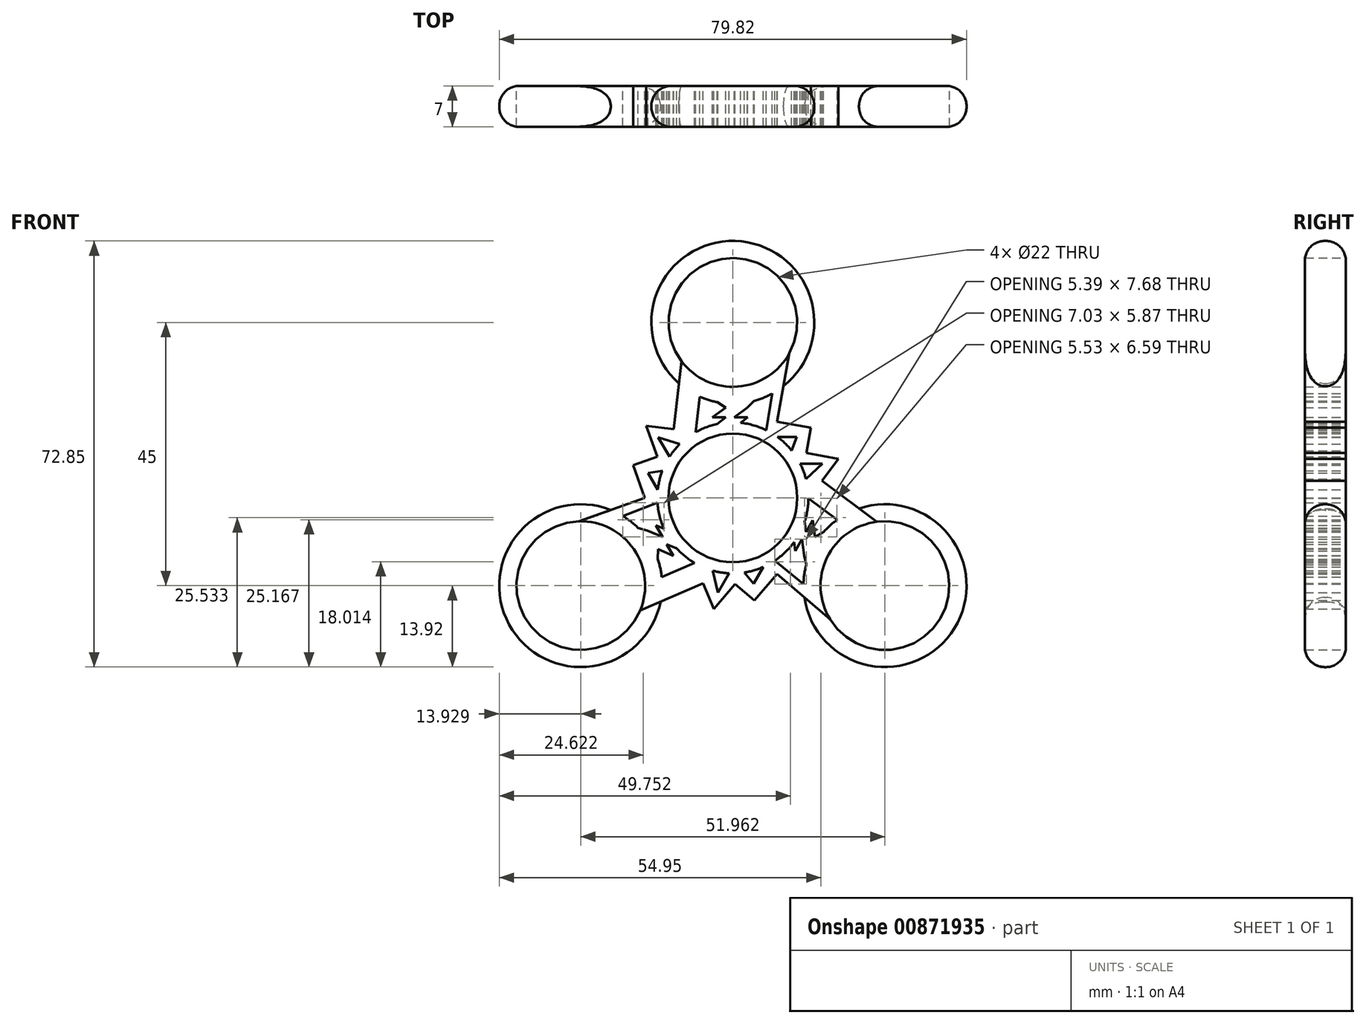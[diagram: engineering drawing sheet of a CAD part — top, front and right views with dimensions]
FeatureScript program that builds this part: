
annotation { "Feature Type Name" : "Feature", "Feature Type Description" : "" }
export const myFeature = defineFeature(function(context is Context, id is Id, definition is map)
    precondition{}
    {
        {
            var Q0;
            Q0=qCreatedBy(makeId("Front.planeOp"),FACE);
            var sketch = newSketch(context, id + "F0", { "sketchPlane" : qUnion([Q0])});
            skCircle(sketch, "E0", {"center": v(0, 0) * mm, "radius": 11 * mm});
            skSolve(sketch);
        }
        {
            var Q0;
            Q0=qCreatedBy(makeId("Front.planeOp"),FACE);
            var sketch = newSketch(context, id + "F1", { "sketchPlane" : qUnion([Q0])});
            skCircle(sketch, "E1", {"center": v(0, 30) * mm, "radius": 11 * mm});
            skCircle(sketch, "E2.1.0", {"center": v(-25.98, -15) * mm, "radius": 11 * mm});
            skCircle(sketch, "E2.2.0", {"center": v(25.98, -15) * mm, "radius": 11 * mm});
            skPoint(sketch, "E2.center", {"position": v(0, 0) * mm});
            skSolve(sketch);
        }
        {
            var Q0;
            Q0=qCreatedBy(makeId("Front.planeOp"),FACE);
            var sketch = newSketch(context, id + "F2", { "sketchPlane" : qUnion([Q0])});
            skArc(sketch, "E3", {"start": v(-2.7, 16.35) * mm, "mid": v(-0.48, 43.92) * mm, "end": v(3.63, 16.57) * mm});
            skLineSegment(sketch, "E4", {"start": v(3.63, 16.57) * mm, "end": v(2.45, 15.46) * mm});
            skLineSegment(sketch, "E5", {"start": v(-2.7, 16.35) * mm, "end": v(-1.21, 15.46) * mm});
            skLineSegment(sketch, "E6", {"start": v(-1.21, 15.46) * mm, "end": v(-2.7, 14.36) * mm});
            skLineSegment(sketch, "E7", {"start": v(2.45, 15.46) * mm, "end": v(0.22, 13.75) * mm});
            skLineSegment(sketch, "E8", {"start": v(0.22, 13.75) * mm, "end": v(2.54, 13.75) * mm});
            skLineSegment(sketch, "E9", {"start": v(-2.7, 14.36) * mm, "end": v(-3.51, 13.75) * mm});
            skLineSegment(sketch, "E10", {"start": v(-3.51, 13.75) * mm, "end": v(-1.21, 13.75) * mm});
            skLineSegment(sketch, "E11", {"start": v(-1.21, 13.75) * mm, "end": v(-2.7, 12.62) * mm});
            skArc(sketch, "E12", {"start": v(-2.7, 12.62) * mm, "mid": v(0.7, -12.88) * mm, "end": v(1.3, 12.84) * mm});
            skLineSegment(sketch, "E13", {"start": v(2.54, 13.75) * mm, "end": v(1.3, 12.84) * mm});
            skArc(sketch, "E14.1.0", {"start": v(-12.82, -10.5) * mm, "mid": v(-37.8, -22.38) * mm, "end": v(-16.17, -5.14) * mm});
            skLineSegment(sketch, "E14.1.1", {"start": v(-12.02, -6.69) * mm, "end": v(-13.18, -4.68) * mm});
            skLineSegment(sketch, "E14.1.2", {"start": v(-14.61, -5.61) * mm, "end": v(-12.02, -6.69) * mm});
            skLineSegment(sketch, "E14.1.3", {"start": v(-16.17, -5.14) * mm, "end": v(-14.61, -5.61) * mm});
            skLineSegment(sketch, "E14.1.4", {"start": v(-11.3, -7.93) * mm, "end": v(-9.58, -8.64) * mm});
            skLineSegment(sketch, "E14.1.5", {"start": v(-13.18, -4.68) * mm, "end": v(-11.77, -5.29) * mm});
            skLineSegment(sketch, "E14.1.6", {"start": v(-12.82, -10.5) * mm, "end": v(-12.78, -8.78) * mm});
            skLineSegment(sketch, "E14.1.7", {"start": v(-10.15, -9.92) * mm, "end": v(-11.3, -7.93) * mm});
            skLineSegment(sketch, "E14.1.8", {"start": v(-12.78, -8.78) * mm, "end": v(-11.1, -9.51) * mm});
            skLineSegment(sketch, "E14.1.9", {"start": v(-11.1, -9.51) * mm, "end": v(-10.15, -9.92) * mm});
            skArc(sketch, "E14.2.0", {"start": v(15.5, -5.85) * mm, "mid": v(38.28, -21.54) * mm, "end": v(12.54, -11.43) * mm});
            skLineSegment(sketch, "E14.2.1", {"start": v(11.8, -7.07) * mm, "end": v(10.64, -9.08) * mm});
            skLineSegment(sketch, "E14.2.2", {"start": v(12.17, -9.85) * mm, "end": v(11.8, -7.07) * mm});
            skLineSegment(sketch, "E14.2.3", {"start": v(12.54, -11.43) * mm, "end": v(12.17, -9.85) * mm});
            skLineSegment(sketch, "E14.2.4", {"start": v(12.52, -5.83) * mm, "end": v(12.27, -3.98) * mm});
            skLineSegment(sketch, "E14.2.5", {"start": v(10.64, -9.08) * mm, "end": v(10.46, -7.55) * mm});
            skLineSegment(sketch, "E14.2.6", {"start": v(15.5, -5.85) * mm, "end": v(14, -6.68) * mm});
            skLineSegment(sketch, "E14.2.7", {"start": v(13.67, -3.83) * mm, "end": v(12.52, -5.83) * mm});
            skLineSegment(sketch, "E14.2.8", {"start": v(14, -6.68) * mm, "end": v(13.79, -4.85) * mm});
            skLineSegment(sketch, "E14.2.9", {"start": v(13.79, -4.85) * mm, "end": v(13.67, -3.83) * mm});
            skSolve(sketch);
        }
        {
            var Q0;
            Q0=qCreatedBy(makeId("Front.planeOp"),FACE);
            var sketch = newSketch(context, id + "F3", { "sketchPlane" : qUnion([Q0])});
            skLineSegment(sketch, "E15", {"start": v(6.74, 17.86) * mm, "end": v(5.69, 11.3) * mm});
            skLineSegment(sketch, "E16", {"start": v(8.66, 19.26) * mm, "end": v(7.53, 13.05) * mm});
            skLineSegment(sketch, "E17", {"start": v(7.53, 13.05) * mm, "end": v(13.35, 11.98) * mm});
            skLineSegment(sketch, "E18", {"start": v(13.35, 11.98) * mm, "end": v(12.56, 7.67) * mm});
            skLineSegment(sketch, "E19", {"start": v(12.56, 7.67) * mm, "end": v(18.04, 6.66) * mm});
            skLineSegment(sketch, "E20", {"start": v(18.04, 6.66) * mm, "end": v(15.23, 2.9) * mm});
            skLineSegment(sketch, "E21", {"start": v(15.23, 2.9) * mm, "end": v(21.78, -2) * mm});
            skLineSegment(sketch, "E22", {"start": v(7.35, 10.42) * mm, "end": v(10.94, 10.42) * mm});
            skLineSegment(sketch, "E23", {"start": v(10.94, 10.42) * mm, "end": v(9.98, 7.88) * mm});
            skLineSegment(sketch, "E24", {"start": v(11.46, 5.87) * mm, "end": v(15.32, 5.87) * mm});
            skLineSegment(sketch, "E25", {"start": v(15.32, 5.87) * mm, "end": v(12.08, 2.9) * mm});
            skLineSegment(sketch, "E26", {"start": v(12.78, 0) * mm, "end": v(18.27, -4.1) * mm});
            skLineSegment(sketch, "E27", {"start": v(6.74, 17.86) * mm, "end": v(8.66, 19.26) * mm});
            skLineSegment(sketch, "E28", {"start": v(5.69, 11.3) * mm, "end": v(7.35, 10.42) * mm});
            skLineSegment(sketch, "E29", {"start": v(9.98, 7.88) * mm, "end": v(11.46, 5.87) * mm});
            skLineSegment(sketch, "E30", {"start": v(12.08, 2.9) * mm, "end": v(12.78, 0) * mm});
            skLineSegment(sketch, "E31", {"start": v(18.27, -4.1) * mm, "end": v(21.78, -2) * mm});
            skLineSegment(sketch, "E32.1.0", {"start": v(-17.05, 5.57) * mm, "end": v(-12.92, 7.04) * mm});
            skLineSegment(sketch, "E32.1.1", {"start": v(-15.06, 0) * mm, "end": v(-17.05, 5.57) * mm});
            skLineSegment(sketch, "E32.1.2", {"start": v(-18.84, -3.1) * mm, "end": v(-12.63, -0.72) * mm});
            skLineSegment(sketch, "E32.1.3", {"start": v(-12.92, 7.04) * mm, "end": v(-14.8, 12.3) * mm});
            skLineSegment(sketch, "E32.1.4", {"start": v(-12.74, 10.33) * mm, "end": v(-8.54, 9.01) * mm});
            skLineSegment(sketch, "E32.1.5", {"start": v(-6.39, 11.07) * mm, "end": v(-5.59, 17.86) * mm});
            skLineSegment(sketch, "E32.1.6", {"start": v(-10.12, 11.74) * mm, "end": v(-9.16, 19.86) * mm});
            skLineSegment(sketch, "E32.1.7", {"start": v(-14.8, 12.3) * mm, "end": v(-10.12, 11.74) * mm});
            skLineSegment(sketch, "E32.1.8", {"start": v(-8.54, 9.01) * mm, "end": v(-6.39, 11.07) * mm});
            skLineSegment(sketch, "E32.1.9", {"start": v(-21.01, -2.13) * mm, "end": v(-15.06, 0) * mm});
            skLineSegment(sketch, "E32.1.10", {"start": v(-12.7, 1.16) * mm, "end": v(-14.5, 4.26) * mm});
            skLineSegment(sketch, "E32.1.11", {"start": v(-5.59, 17.86) * mm, "end": v(-9.16, 19.86) * mm});
            skLineSegment(sketch, "E32.1.12", {"start": v(-10.81, 7) * mm, "end": v(-12.74, 10.33) * mm});
            skLineSegment(sketch, "E32.1.13", {"start": v(-14.5, 4.26) * mm, "end": v(-11.81, 4.7) * mm});
            skLineSegment(sketch, "E32.1.14", {"start": v(-18.84, -3.1) * mm, "end": v(-21.01, -2.13) * mm});
            skLineSegment(sketch, "E32.1.15", {"start": v(-11.81, 4.7) * mm, "end": v(-10.81, 7) * mm});
            skLineSegment(sketch, "E32.1.16", {"start": v(-12.63, -0.72) * mm, "end": v(-12.7, 1.16) * mm});
            skLineSegment(sketch, "E32.2.0", {"start": v(3.7, -17.55) * mm, "end": v(0.36, -14.7) * mm});
            skLineSegment(sketch, "E32.2.1", {"start": v(7.54, -13.04) * mm, "end": v(3.7, -17.55) * mm});
            skLineSegment(sketch, "E32.2.2", {"start": v(12.1, -14.77) * mm, "end": v(6.94, -10.57) * mm});
            skLineSegment(sketch, "E32.2.3", {"start": v(0.36, -14.7) * mm, "end": v(-3.25, -18.95) * mm});
            skLineSegment(sketch, "E32.2.4", {"start": v(-2.58, -16.2) * mm, "end": v(-3.53, -11.9) * mm});
            skLineSegment(sketch, "E32.2.5", {"start": v(-6.39, -11.07) * mm, "end": v(-12.68, -13.77) * mm});
            skLineSegment(sketch, "E32.2.6", {"start": v(-5.1, -14.63) * mm, "end": v(-12.62, -17.87) * mm});
            skLineSegment(sketch, "E32.2.7", {"start": v(-3.25, -18.95) * mm, "end": v(-5.1, -14.63) * mm});
            skLineSegment(sketch, "E32.2.8", {"start": v(-3.53, -11.9) * mm, "end": v(-6.39, -11.07) * mm});
            skLineSegment(sketch, "E32.2.9", {"start": v(12.35, -17.13) * mm, "end": v(7.54, -13.04) * mm});
            skLineSegment(sketch, "E32.2.10", {"start": v(5.35, -11.58) * mm, "end": v(3.56, -14.68) * mm});
            skLineSegment(sketch, "E32.2.11", {"start": v(-12.68, -13.77) * mm, "end": v(-12.62, -17.87) * mm});
            skLineSegment(sketch, "E32.2.12", {"start": v(-0.65, -12.86) * mm, "end": v(-2.58, -16.2) * mm});
            skLineSegment(sketch, "E32.2.13", {"start": v(3.56, -14.68) * mm, "end": v(1.84, -12.58) * mm});
            skLineSegment(sketch, "E32.2.14", {"start": v(12.1, -14.77) * mm, "end": v(12.35, -17.13) * mm});
            skLineSegment(sketch, "E32.2.15", {"start": v(1.84, -12.58) * mm, "end": v(-0.65, -12.86) * mm});
            skLineSegment(sketch, "E32.2.16", {"start": v(6.94, -10.57) * mm, "end": v(5.35, -11.58) * mm});
            skPoint(sketch, "E32.center", {"position": v(0, 0) * mm});
            skSolve(sketch);
        }
        {
            var Q0;
            Q0 = qSketchRegion(id + "F2", true);
            var Q1;
            Q1 = qSketchRegion(id + "F3", true);
            extrude(context, id + "F4", {"entities" : qUnion([Q0, Q1]), "depth" : 7 * mm, "offsetDistance" : 25 * mm});
        }
        {
            var Q0;
            Q0=makeQuery(id+"F4.opExtrude","SWEPT_BODY",BODY,{"disambiguationData":[OSD([sQuery(id+"F2.wireOp",EDGE,"E3"),sQuery(id+"F2.wireOp",EDGE,"E4"),sQuery(id+"F2.wireOp",EDGE,"E5"),sQuery(id+"F2.wireOp",EDGE,"E6"),sQuery(id+"F2.wireOp",EDGE,"E7"),sQuery(id+"F2.wireOp",EDGE,"E8"),sQuery(id+"F2.wireOp",EDGE,"E9"),sQuery(id+"F2.wireOp",EDGE,"E10"),sQuery(id+"F2.wireOp",EDGE,"E11"),sQuery(id+"F2.wireOp",EDGE,"E12"),sQuery(id+"F2.wireOp",EDGE,"E13"),sQuery(id+"F2.wireOp",EDGE,"E14.1.0"),sQuery(id+"F2.wireOp",EDGE,"E14.1.1"),sQuery(id+"F2.wireOp",EDGE,"E14.1.2"),sQuery(id+"F2.wireOp",EDGE,"E14.1.3"),sQuery(id+"F2.wireOp",EDGE,"E14.1.4"),sQuery(id+"F2.wireOp",EDGE,"E14.1.5"),sQuery(id+"F2.wireOp",EDGE,"E14.1.6"),sQuery(id+"F2.wireOp",EDGE,"E14.1.7"),sQuery(id+"F2.wireOp",EDGE,"E14.1.8"),sQuery(id+"F2.wireOp",EDGE,"E14.1.9"),sQuery(id+"F2.wireOp",EDGE,"E14.2.0"),sQuery(id+"F2.wireOp",EDGE,"E14.2.1"),sQuery(id+"F2.wireOp",EDGE,"E14.2.2"),sQuery(id+"F2.wireOp",EDGE,"E14.2.3"),sQuery(id+"F2.wireOp",EDGE,"E14.2.4"),sQuery(id+"F2.wireOp",EDGE,"E14.2.5"),sQuery(id+"F2.wireOp",EDGE,"E14.2.6"),sQuery(id+"F2.wireOp",EDGE,"E14.2.7"),sQuery(id+"F2.wireOp",EDGE,"E14.2.8"),sQuery(id+"F2.wireOp",EDGE,"E14.2.9")])]});
            var Q1;
            Q1=makeQuery(id+"F4.opExtrude","SWEPT_BODY",BODY,{"disambiguationData":[OSD([sQuery(id+"F3.wireOp",EDGE,"E15"),sQuery(id+"F3.wireOp",EDGE,"E16"),sQuery(id+"F3.wireOp",EDGE,"E17"),sQuery(id+"F3.wireOp",EDGE,"E18"),sQuery(id+"F3.wireOp",EDGE,"E19"),sQuery(id+"F3.wireOp",EDGE,"E20"),sQuery(id+"F3.wireOp",EDGE,"E21"),sQuery(id+"F3.wireOp",EDGE,"E22"),sQuery(id+"F3.wireOp",EDGE,"E23"),sQuery(id+"F3.wireOp",EDGE,"E24"),sQuery(id+"F3.wireOp",EDGE,"E25"),sQuery(id+"F3.wireOp",EDGE,"E26"),sQuery(id+"F3.wireOp",EDGE,"E27"),sQuery(id+"F3.wireOp",EDGE,"E28"),sQuery(id+"F3.wireOp",EDGE,"E29"),sQuery(id+"F3.wireOp",EDGE,"E30"),sQuery(id+"F3.wireOp",EDGE,"E31")])]});
            var Q2;
            Q2=makeQuery(id+"F4.opExtrude","SWEPT_BODY",BODY,{"disambiguationData":[OSD([sQuery(id+"F3.wireOp",EDGE,"E32.1.0"),sQuery(id+"F3.wireOp",EDGE,"E32.1.1"),sQuery(id+"F3.wireOp",EDGE,"E32.1.2"),sQuery(id+"F3.wireOp",EDGE,"E32.1.3"),sQuery(id+"F3.wireOp",EDGE,"E32.1.4"),sQuery(id+"F3.wireOp",EDGE,"E32.1.5"),sQuery(id+"F3.wireOp",EDGE,"E32.1.6"),sQuery(id+"F3.wireOp",EDGE,"E32.1.7"),sQuery(id+"F3.wireOp",EDGE,"E32.1.8"),sQuery(id+"F3.wireOp",EDGE,"E32.1.9"),sQuery(id+"F3.wireOp",EDGE,"E32.1.10"),sQuery(id+"F3.wireOp",EDGE,"E32.1.11"),sQuery(id+"F3.wireOp",EDGE,"E32.1.12"),sQuery(id+"F3.wireOp",EDGE,"E32.1.13"),sQuery(id+"F3.wireOp",EDGE,"E32.1.14"),sQuery(id+"F3.wireOp",EDGE,"E32.1.15"),sQuery(id+"F3.wireOp",EDGE,"E32.1.16")])]});
            var Q3;
            Q3=makeQuery(id+"F4.opExtrude","SWEPT_BODY",BODY,{"disambiguationData":[OSD([sQuery(id+"F3.wireOp",EDGE,"E32.2.0"),sQuery(id+"F3.wireOp",EDGE,"E32.2.1"),sQuery(id+"F3.wireOp",EDGE,"E32.2.2"),sQuery(id+"F3.wireOp",EDGE,"E32.2.3"),sQuery(id+"F3.wireOp",EDGE,"E32.2.4"),sQuery(id+"F3.wireOp",EDGE,"E32.2.5"),sQuery(id+"F3.wireOp",EDGE,"E32.2.6"),sQuery(id+"F3.wireOp",EDGE,"E32.2.7"),sQuery(id+"F3.wireOp",EDGE,"E32.2.8"),sQuery(id+"F3.wireOp",EDGE,"E32.2.9"),sQuery(id+"F3.wireOp",EDGE,"E32.2.10"),sQuery(id+"F3.wireOp",EDGE,"E32.2.11"),sQuery(id+"F3.wireOp",EDGE,"E32.2.12"),sQuery(id+"F3.wireOp",EDGE,"E32.2.13"),sQuery(id+"F3.wireOp",EDGE,"E32.2.14"),sQuery(id+"F3.wireOp",EDGE,"E32.2.15"),sQuery(id+"F3.wireOp",EDGE,"E32.2.16")])]});
            booleanBodies(context, id + "F5", {"operationType" : BooleanOperationType.UNION, "tools" : qUnion([Q0, Q1, Q2, Q3])});
        }
        {
            var Q0;
            Q0=makeQuery(id+"F1.imprint","IMPRINT",FACE,{"disambiguationData":[TD([[makeQuery(id+"F1.imprint","IMPRINT",EDGE,{"derivedFrom":sQuery(id+"F1.wireOp",EDGE,"E2.2.0")}),1.0]])]});
            extrude(context, id + "F6", {"entities" : qUnion([Q0]), "operationType" : NewBodyOperationType.REMOVE, "depth" : 7 * mm, "offsetDistance" : 25 * mm});
        }
        {
            var Q0;
            Q0=makeQuery(id+"F0.imprint","IMPRINT",FACE,{"disambiguationData":[TD([[makeQuery(id+"F0.imprint","IMPRINT",EDGE,{"derivedFrom":sQuery(id+"F0.wireOp",EDGE,"E0")}),1.0]])]});
            extrude(context, id + "F7", {"entities" : qUnion([Q0]), "operationType" : NewBodyOperationType.ADD, "depth" : 7 * mm, "offsetDistance" : 25 * mm});
        }
        {
            var Q0;
            Q0 = qSketchRegion(id + "F0", true);
            extrude(context, id + "F8", {"entities" : qUnion([Q0]), "operationType" : NewBodyOperationType.REMOVE, "depth" : 7 * mm, "offsetDistance" : 25 * mm});
        }
        {
            var Q0;
            Q0=makeQuery(id+"F1.imprint","IMPRINT",FACE,{"disambiguationData":[TD([[makeQuery(id+"F1.imprint","IMPRINT",EDGE,{"derivedFrom":sQuery(id+"F1.wireOp",EDGE,"E1")}),1.0]])]});
            extrude(context, id + "F9", {"entities" : qUnion([Q0]), "operationType" : NewBodyOperationType.REMOVE, "depth" : 7 * mm, "offsetDistance" : 25 * mm});
        }
        {
            var Q0;
            Q0=makeQuery(id+"F1.imprint","IMPRINT",FACE,{"disambiguationData":[TD([[makeQuery(id+"F1.imprint","IMPRINT",EDGE,{"derivedFrom":sQuery(id+"F1.wireOp",EDGE,"E2.1.0")}),1.0]])]});
            extrude(context, id + "F10", {"entities" : qUnion([Q0]), "operationType" : NewBodyOperationType.REMOVE, "depth" : 7 * mm, "offsetDistance" : 25 * mm});
        }
        {
            var Q0;
            {var subQ0=sQuery(id+"F3.wireOp",EDGE,"E16");var subQ1=sQuery(id+"F2.wireOp",EDGE,"E3");Q0=makeQuery(id+"F5.opBoolean","SPLIT",EDGE,{"disambiguationData":[TD([makeQuery(id+"F4.opExtrude","SWEPT_FACE",FACE,{"disambiguationData":[OSD([subQ0])]})])],"derivedFrom":makeQuery(id+"F4.opExtrude","CAP_EDGE",EDGE,{"disambiguationData":[OSD([subQ1])],"isStart":true})});}
            var Q1;
            {var subQ0=sQuery(id+"F3.wireOp",EDGE,"E16");var subQ1=sQuery(id+"F2.wireOp",EDGE,"E3");Q1=makeQuery(id+"F5.opBoolean","SPLIT",EDGE,{"disambiguationData":[TD([makeQuery(id+"F4.opExtrude","SWEPT_FACE",FACE,{"disambiguationData":[OSD([subQ0])]})])],"derivedFrom":makeQuery(id+"F4.opExtrude","CAP_EDGE",EDGE,{"disambiguationData":[OSD([subQ1])],"isStart":false})});}
            var Q2;
            {var subQ0=sQuery(id+"F3.wireOp",EDGE,"E21");var subQ1=sQuery(id+"F2.wireOp",EDGE,"E14.2.0");Q2=makeQuery(id+"F5.opBoolean","SPLIT",EDGE,{"disambiguationData":[TD([makeQuery(id+"F4.opExtrude","SWEPT_FACE",FACE,{"disambiguationData":[OSD([subQ0])]})])],"derivedFrom":makeQuery(id+"F4.opExtrude","CAP_EDGE",EDGE,{"disambiguationData":[OSD([subQ1])],"isStart":false})});}
            var Q3;
            {var subQ0=sQuery(id+"F3.wireOp",EDGE,"E21");var subQ1=sQuery(id+"F2.wireOp",EDGE,"E14.2.0");Q3=makeQuery(id+"F5.opBoolean","SPLIT",EDGE,{"disambiguationData":[TD([makeQuery(id+"F4.opExtrude","SWEPT_FACE",FACE,{"disambiguationData":[OSD([subQ0])]})])],"derivedFrom":makeQuery(id+"F4.opExtrude","CAP_EDGE",EDGE,{"disambiguationData":[OSD([subQ1])],"isStart":true})});}
            var Q4;
            {var subQ0=sQuery(id+"F3.wireOp",EDGE,"E32.1.9");var subQ1=sQuery(id+"F2.wireOp",EDGE,"E14.1.0");Q4=makeQuery(id+"F5.opBoolean","SPLIT",EDGE,{"disambiguationData":[TD([makeQuery(id+"F4.opExtrude","SWEPT_FACE",FACE,{"disambiguationData":[OSD([subQ0])]})])],"derivedFrom":makeQuery(id+"F4.opExtrude","CAP_EDGE",EDGE,{"disambiguationData":[OSD([subQ1])],"isStart":true})});}
            var Q5;
            {var subQ0=sQuery(id+"F3.wireOp",EDGE,"E32.1.9");var subQ2=sQuery(id+"F2.wireOp",EDGE,"E14.1.0");Q5=makeQuery(id+"F5.opBoolean","SPLIT",EDGE,{"disambiguationData":[TD([makeQuery(id+"F4.opExtrude","SWEPT_FACE",FACE,{"disambiguationData":[OSD([subQ0])]})])],"derivedFrom":makeQuery(id+"F4.opExtrude","CAP_EDGE",EDGE,{"disambiguationData":[OSD([subQ2])],"isStart":false})});}
            fillet(context, id + "F11", {"entities" : qUnion([Q0, Q1, Q2, Q3, Q4, Q5]), "radius" : 3.4 * mm, "tangentPropagation" : true, "allowEdgeOverflow" : false});
        }
    });
